# Revit family: Vandal_Resistant_ Square_Rectangular_Downpipe
name_source: partatom
category: Plumbing Fixtures
revit_build: Autodesk Revit 2013 (Build: 20130531_2115(x64)
units: mm (PartAtom-declared; Revit-internal decimal feet)

## types (3) — shared parameters
Assembly Code = D2040
Available Colours = http://www.marleyalutec.co.uk
Default Elevation = 1219 mm
Description = Vandal Resistant Square Rectangular Downpipe
DocumentationLink URL = http://www.marleyalutec.co.uk
ExpectedLife = 50
Keynote = R10/350
Manufacturer = Marley Alutec
Model = Vandal Resistant Square Rectangular Downpipe
Name = Vandal Resistant Square Rectangular Downpipe
Product Documentation Link = http://www.marleyalutec.co.uk
Product Page URL = http://www.marleyalutec.co.uk
Product Specification Link = http://www.marleyalutec.co.uk
Type Comments = Vandal Resistant Square Rectangular Downpipe
TypeName = Vandal Resistant Square Rectangular Downpipe
URL = http://www.marleyalutec.co.uk
Uniclass2 = Ss-50-30-02-28
_current revision = 1
_distributed by = www.bimstore.co.uk
zero-valued in all types: _BIMspec_GUID

## per-type parameters (varying)
| type | 102x102mm | 102x76mm | 72x72mm | Inner Length | Inner Width | ModelNumber | Outter Length | Outter Width | Product Code | Shoe Type | Size |
| 72x72mm | No | No | Yes | 70 mm | 70 mm | RVR311 (1m) RVR312 (2m) RVR313 (3m) | 72 mm  [stored 0.23622 ft] | 72 mm  [stored 0.23622 ft] | RVR311 (1m) RVR312 (2m) RVR313 (3m) | Vandal Resistant Shoe all sizes : 72 x 72 | 72x72 |
| 102x76mm | No | Yes | No | 74 mm | 100 mm  [stored 0.328084 ft] | RVR111 (1m) RVR112 (2m) RVR113 (3m) | 76 mm  [stored 0.249344 ft] | 102 mm  [stored 0.334646 ft] | RVR111 (1m) RVR112 (2m) RVR113 (3m) | Vandal Resistant Shoe all sizes : 102 x 76 | 102x76 |
| 102x102mm | Yes | No | No | 100 mm  [stored 0.328084 ft] | 100 mm  [stored 0.328084 ft] | RVR411 (1m) RVR412 (2m) RVR 413 (3m) | 102 mm  [stored 0.334646 ft] | 102 mm  [stored 0.334646 ft] | RVR411 (1m) RVR412 (2m) RVR 413 (3m) | Vandal Resistant Shoe all sizes : 102 x 102 | 102x102 |

note: [stored X ft] marks values corroborated as IEEE doubles in the binary element streams (Revit-internal decimal feet)

## geometry (parser evidence)
native form markers: Blend x4, Sweep x2
no freeform markers — native parametric forms only
